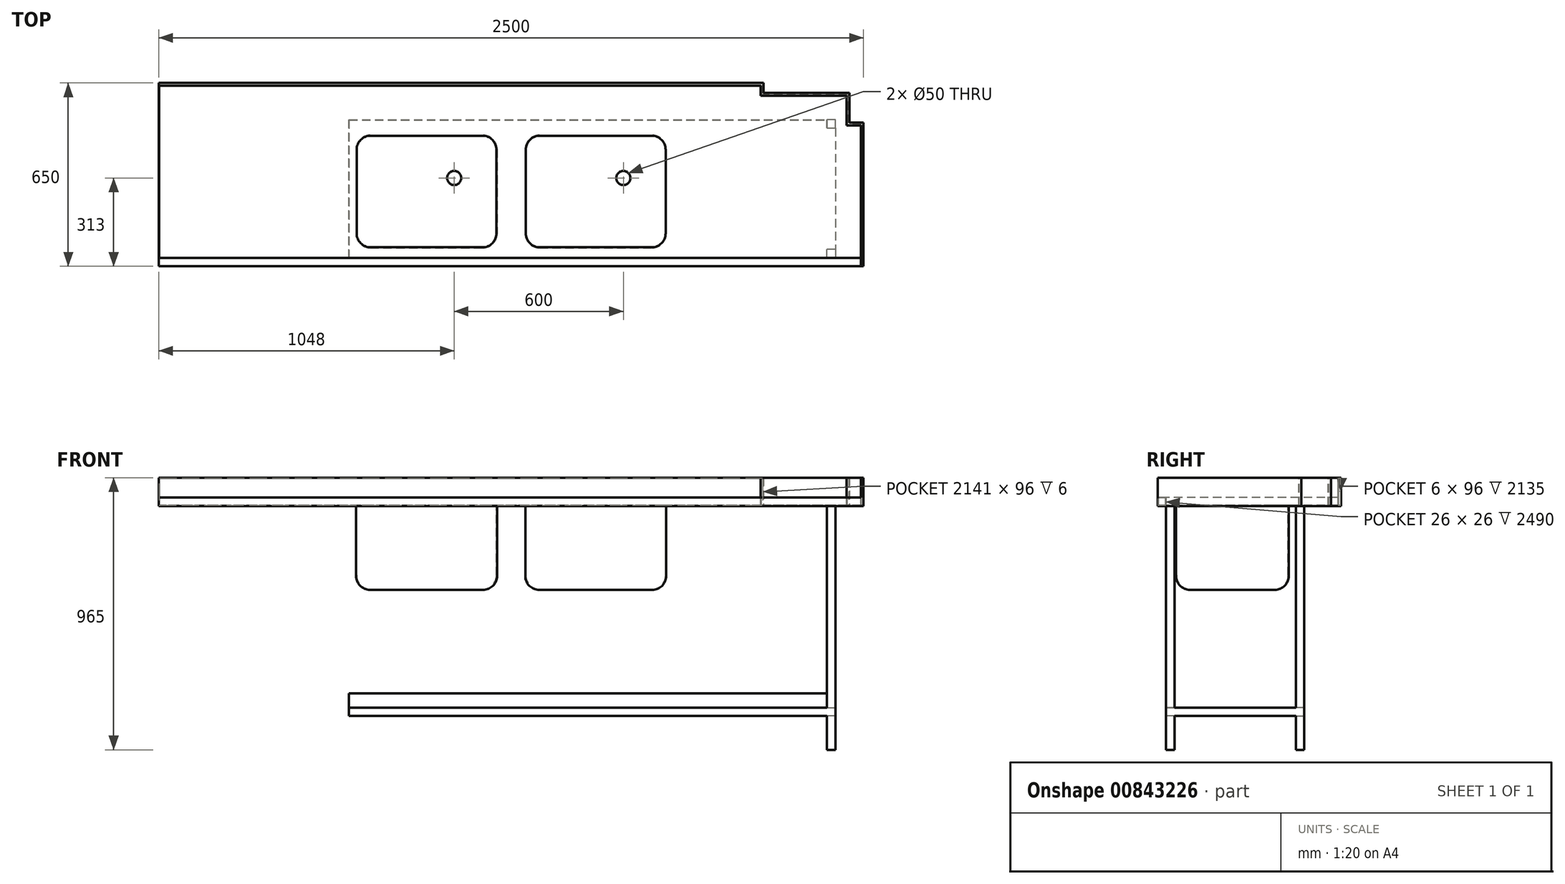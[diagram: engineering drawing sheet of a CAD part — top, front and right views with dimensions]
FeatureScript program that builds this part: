
annotation { "Feature Type Name" : "Feature", "Feature Type Description" : "" }
export const myFeature = defineFeature(function(context is Context, id is Id, definition is map)
    precondition{}
    {
        {
            var Q0;
            Q0=qCreatedBy(makeId("Top.planeOp"),FACE);
            var sketch = newSketch(context, id + "F0", { "sketchPlane" : qUnion([Q0])});
            skLineSegment(sketch, "E0", {"start": v(0, 0) * mm, "end": v(2500, 0) * mm});
            skLineSegment(sketch, "E1", {"start": v(2500, 0) * mm, "end": v(2500, 510) * mm});
            skLineSegment(sketch, "E2", {"start": v(2500, 510) * mm, "end": v(2450, 510) * mm});
            skLineSegment(sketch, "E3", {"start": v(2450, 510) * mm, "end": v(2450, 615) * mm});
            skLineSegment(sketch, "E4", {"start": v(2450, 615) * mm, "end": v(2145, 615) * mm});
            skLineSegment(sketch, "E5", {"start": v(2145, 615) * mm, "end": v(2145, 650) * mm});
            skLineSegment(sketch, "E6", {"start": v(2145, 650) * mm, "end": v(0, 650) * mm});
            skLineSegment(sketch, "E7", {"start": v(0, 650) * mm, "end": v(0, 0) * mm});
            skSolve(sketch);
        }
        {
            var Q0;
            Q0 = qSketchRegion(id + "F0", true);
            extrude(context, id + "F1", {"entities" : qUnion([Q0]), "depth" : 100 * mm, "offsetDistance" : 25 * mm});
        }
        {
            var Q0;
            Q0=makeQuery(id+"F1.opExtrude","CAP_FACE",FACE,{"disambiguationData":[OSD([sQuery(id+"F0.wireOp",EDGE,"E0"),sQuery(id+"F0.wireOp",EDGE,"E1"),sQuery(id+"F0.wireOp",EDGE,"E2"),sQuery(id+"F0.wireOp",EDGE,"E3"),sQuery(id+"F0.wireOp",EDGE,"E4"),sQuery(id+"F0.wireOp",EDGE,"E5"),sQuery(id+"F0.wireOp",EDGE,"E6"),sQuery(id+"F0.wireOp",EDGE,"E7")])],"isStart":false});
            var sketch = newSketch(context, id + "F2", { "sketchPlane" : qUnion([Q0])});
            skLineSegment(sketch, "E8", {"start": v(0, 30) * mm, "end": v(2490, 30) * mm});
            skLineSegment(sketch, "E9", {"start": v(2490, 500) * mm, "end": v(2440, 500) * mm});
            skLineSegment(sketch, "E10", {"start": v(2440, 500) * mm, "end": v(2440, 605) * mm});
            skLineSegment(sketch, "E11", {"start": v(2440, 605) * mm, "end": v(2135, 605) * mm});
            skLineSegment(sketch, "E12", {"start": v(2135, 605) * mm, "end": v(2135, 640) * mm});
            skLineSegment(sketch, "E13", {"start": v(2135, 640) * mm, "end": v(0, 640) * mm});
            skLineSegment(sketch, "E14", {"start": v(0, 640) * mm, "end": v(0, 30) * mm});
            skLineSegment(sketch, "E15", {"start": v(2490, 500) * mm, "end": v(2490, 30) * mm});
            skSolve(sketch);
        }
        {
            var Q0;
            Q0 = qSketchRegion(id + "F2", true);
            extrude(context, id + "F3", {"entities" : qUnion([Q0]), "operationType" : NewBodyOperationType.REMOVE, "oppositeDirection" : true, "depth" : 98 * mm, "offsetDistance" : 25 * mm});
        }
        {
            var Q0;
            Q0=makeQuery(id+"F3.boolean.opBoolean","COPY",FACE,{"derivedFrom":makeQuery(id+"F3.opExtrude","CAP_FACE",FACE,{"disambiguationData":[OSD([sQuery(id+"F2.wireOp",EDGE,"E8"),sQuery(id+"F2.wireOp",EDGE,"WZKGSPdI-TEh4-vyXV-Ibzs-68OWXZtWBOVU"),sQuery(id+"F2.wireOp",EDGE,"E9"),sQuery(id+"F2.wireOp",EDGE,"E10"),sQuery(id+"F2.wireOp",EDGE,"E11"),sQuery(id+"F2.wireOp",EDGE,"E12"),sQuery(id+"F2.wireOp",EDGE,"E13"),sQuery(id+"F2.wireOp",EDGE,"E14")])],"isStart":false})});
            var sketch = newSketch(context, id + "F4", { "sketchPlane" : qUnion([Q0])});
            skLineSegment(sketch, "E16.bottom", {"start": v(700, 465) * mm, "end": v(1200, 465) * mm});
            skLineSegment(sketch, "E16.top", {"start": v(700, 65) * mm, "end": v(1200, 65) * mm});
            skLineSegment(sketch, "E16.left", {"start": v(700, 465) * mm, "end": v(700, 65) * mm});
            skLineSegment(sketch, "E16.right", {"start": v(1200, 465) * mm, "end": v(1200, 65) * mm});
            skLineSegment(sketch, "E17.bottom", {"start": v(1300, 465) * mm, "end": v(1800, 465) * mm});
            skLineSegment(sketch, "E17.top", {"start": v(1300, 65) * mm, "end": v(1800, 65) * mm});
            skLineSegment(sketch, "E17.left", {"start": v(1300, 465) * mm, "end": v(1300, 65) * mm});
            skLineSegment(sketch, "E17.right", {"start": v(1800, 465) * mm, "end": v(1800, 65) * mm});
            skSolve(sketch);
        }
        {
            var Q0;
            Q0 = qSketchRegion(id + "F4", true);
            var Q1;
            Q1=makeQuery(id+"F4.imprint","IMPRINT",FACE,{"disambiguationData":[TD([[makeQuery(id+"F4.imprint","IMPRINT",EDGE,{"derivedFrom":sQuery(id+"F4.wireOp",EDGE,"0PvLLEWH-obXo-W6PY-pfR3-ScPsw102PUe8.bottom")}),-1.0]])]});
            var Q2;
            Q2=makeQuery(id+"F4.imprint","IMPRINT",FACE,{"disambiguationData":[TD([[makeQuery(id+"F4.imprint","IMPRINT",EDGE,{"derivedFrom":sQuery(id+"F4.wireOp",EDGE,"tlFFw7kf-LK7W-eKNi-DYG7-TUnyD2dlcll0.bottom")}),-1.0]])]});
            extrude(context, id + "F5", {"entities" : qUnion([Q0, Q1, Q2]), "operationType" : NewBodyOperationType.ADD, "oppositeDirection" : true, "depth" : 300 * mm, "offsetDistance" : 25 * mm});
        }
        {
            var Q0;
            Q0=makeQuery(id+"F1.opExtrude","CAP_FACE",FACE,{"disambiguationData":[OSD([sQuery(id+"F0.wireOp",EDGE,"E0"),sQuery(id+"F0.wireOp",EDGE,"E1"),sQuery(id+"F0.wireOp",EDGE,"E2"),sQuery(id+"F0.wireOp",EDGE,"E3"),sQuery(id+"F0.wireOp",EDGE,"E4"),sQuery(id+"F0.wireOp",EDGE,"E5"),sQuery(id+"F0.wireOp",EDGE,"E6"),sQuery(id+"F0.wireOp",EDGE,"E7")])],"isStart":false});
            var sketch = newSketch(context, id + "F6", { "sketchPlane" : qUnion([Q0])});
            skLineSegment(sketch, "E18.bottom", {"start": v(0, 30) * mm, "end": v(2490, 30) * mm});
            skLineSegment(sketch, "E18.top", {"start": v(0, 0) * mm, "end": v(2490, 0) * mm});
            skLineSegment(sketch, "E18.left", {"start": v(0, 30) * mm, "end": v(0, 0) * mm});
            skLineSegment(sketch, "E18.right", {"start": v(2490, 30) * mm, "end": v(2490, 0) * mm});
            skSolve(sketch);
        }
        {
            var Q0;
            Q0 = qSketchRegion(id + "F6", true);
            extrude(context, id + "F7", {"entities" : qUnion([Q0]), "operationType" : NewBodyOperationType.REMOVE, "oppositeDirection" : true, "depth" : 70 * mm, "offsetDistance" : 25 * mm});
        }
        {
            var Q0;
            Q0=makeQuery(id+"F3.boolean.opBoolean","COPY",FACE,{"derivedFrom":makeQuery(id+"F3.opExtrude","CAP_FACE",FACE,{"disambiguationData":[OSD([sQuery(id+"F2.wireOp",EDGE,"E8"),sQuery(id+"F2.wireOp",EDGE,"WZKGSPdI-TEh4-vyXV-Ibzs-68OWXZtWBOVU"),sQuery(id+"F2.wireOp",EDGE,"E9"),sQuery(id+"F2.wireOp",EDGE,"E10"),sQuery(id+"F2.wireOp",EDGE,"E11"),sQuery(id+"F2.wireOp",EDGE,"E12"),sQuery(id+"F2.wireOp",EDGE,"E13"),sQuery(id+"F2.wireOp",EDGE,"E14")])],"isStart":false})});
            shell(context, id + "F8", {"entities" : qUnion([Q0]), "thickness" : 2 * mm});
        }
        {
            var Q0;
            Q0=makeQuery(id+"F8.opShell","OFFSET_EDGE",EDGE,{"disambiguationData":[OSD([sQuery(id+"F4.wireOp",EDGE,"E16.bottom"),sQuery(id+"F4.wireOp",EDGE,"E16.left")])]});
            var Q1;
            Q1=makeQuery(id+"F8.opShell","OFFSET_EDGE",EDGE,{"disambiguationData":[OSD([sQuery(id+"F4.wireOp",EDGE,"E16.bottom"),sQuery(id+"F4.wireOp",EDGE,"E16.right")])]});
            var Q2;
            Q2=makeQuery(id+"F8.opShell","OFFSET_EDGE",EDGE,{"disambiguationData":[OSD([sQuery(id+"F4.wireOp",EDGE,"E16.bottom")])]});
            var Q3;
            Q3=makeQuery(id+"F8.opShell","OFFSET_EDGE",EDGE,{"disambiguationData":[OSD([sQuery(id+"F4.wireOp",EDGE,"E16.top"),sQuery(id+"F4.wireOp",EDGE,"E16.left")])]});
            var Q4;
            Q4=makeQuery(id+"F8.opShell","OFFSET_EDGE",EDGE,{"disambiguationData":[OSD([sQuery(id+"F4.wireOp",EDGE,"E16.top"),sQuery(id+"F4.wireOp",EDGE,"E16.right")])]});
            var Q5;
            Q5=makeQuery(id+"F8.opShell","OFFSET_EDGE",EDGE,{"disambiguationData":[OSD([sQuery(id+"F4.wireOp",EDGE,"E16.right")])]});
            var Q6;
            Q6=makeQuery(id+"F8.opShell","OFFSET_EDGE",EDGE,{"disambiguationData":[OSD([sQuery(id+"F4.wireOp",EDGE,"E16.top")])]});
            var Q7;
            Q7=makeQuery(id+"F8.opShell","OFFSET_EDGE",EDGE,{"disambiguationData":[OSD([sQuery(id+"F4.wireOp",EDGE,"E16.left")])]});
            var Q8;
            Q8=makeQuery(id+"F8.opShell","OFFSET_EDGE",EDGE,{"disambiguationData":[OSD([sQuery(id+"F4.wireOp",EDGE,"E17.left")])]});
            var Q9;
            Q9=makeQuery(id+"F8.opShell","OFFSET_EDGE",EDGE,{"disambiguationData":[OSD([sQuery(id+"F4.wireOp",EDGE,"E17.bottom"),sQuery(id+"F4.wireOp",EDGE,"E17.left")])]});
            var Q10;
            Q10=makeQuery(id+"F8.opShell","OFFSET_EDGE",EDGE,{"disambiguationData":[OSD([sQuery(id+"F4.wireOp",EDGE,"E17.bottom")])]});
            var Q11;
            Q11=makeQuery(id+"F8.opShell","OFFSET_EDGE",EDGE,{"disambiguationData":[OSD([sQuery(id+"F4.wireOp",EDGE,"E17.bottom"),sQuery(id+"F4.wireOp",EDGE,"E17.right")])]});
            var Q12;
            Q12=makeQuery(id+"F8.opShell","OFFSET_EDGE",EDGE,{"disambiguationData":[OSD([sQuery(id+"F4.wireOp",EDGE,"E17.right")])]});
            var Q13;
            Q13=makeQuery(id+"F8.opShell","OFFSET_EDGE",EDGE,{"disambiguationData":[OSD([sQuery(id+"F4.wireOp",EDGE,"E17.top"),sQuery(id+"F4.wireOp",EDGE,"E17.right")])]});
            var Q14;
            Q14=makeQuery(id+"F8.opShell","OFFSET_EDGE",EDGE,{"disambiguationData":[OSD([sQuery(id+"F4.wireOp",EDGE,"E17.top")])]});
            var Q15;
            Q15=makeQuery(id+"F8.opShell","OFFSET_EDGE",EDGE,{"disambiguationData":[OSD([sQuery(id+"F4.wireOp",EDGE,"E17.top"),sQuery(id+"F4.wireOp",EDGE,"E17.left")])]});
            var Q16;
            Q16=makeQuery(id+"F5.opExtrude","SWEPT_EDGE",EDGE,{"disambiguationData":[OSD([sQuery(id+"F4.wireOp",EDGE,"E16.top"),sQuery(id+"F4.wireOp",EDGE,"E16.left")])]});
            var Q17;
            Q17=makeQuery(id+"F5.opExtrude","CAP_EDGE",EDGE,{"disambiguationData":[OSD([sQuery(id+"F4.wireOp",EDGE,"E16.left")])],"isStart":false});
            var Q18;
            Q18=makeQuery(id+"F5.opExtrude","CAP_EDGE",EDGE,{"disambiguationData":[OSD([sQuery(id+"F4.wireOp",EDGE,"E16.top")])],"isStart":false});
            var Q19;
            Q19=makeQuery(id+"F5.opExtrude","SWEPT_EDGE",EDGE,{"disambiguationData":[OSD([sQuery(id+"F4.wireOp",EDGE,"E17.top"),sQuery(id+"F4.wireOp",EDGE,"E17.left")])]});
            var Q20;
            Q20=makeQuery(id+"F5.opExtrude","CAP_EDGE",EDGE,{"disambiguationData":[OSD([sQuery(id+"F4.wireOp",EDGE,"E17.left")])],"isStart":false});
            var Q21;
            Q21=makeQuery(id+"F5.opExtrude","CAP_EDGE",EDGE,{"disambiguationData":[OSD([sQuery(id+"F4.wireOp",EDGE,"E17.top")])],"isStart":false});
            var Q22;
            Q22=makeQuery(id+"F5.opExtrude","SWEPT_EDGE",EDGE,{"disambiguationData":[OSD([sQuery(id+"F4.wireOp",EDGE,"E16.top"),sQuery(id+"F4.wireOp",EDGE,"E16.right")])]});
            var Q23;
            Q23=makeQuery(id+"F5.opExtrude","CAP_EDGE",EDGE,{"disambiguationData":[OSD([sQuery(id+"F4.wireOp",EDGE,"E16.right")])],"isStart":false});
            var Q24;
            Q24=makeQuery(id+"F5.opExtrude","SWEPT_EDGE",EDGE,{"disambiguationData":[OSD([sQuery(id+"F4.wireOp",EDGE,"E17.top"),sQuery(id+"F4.wireOp",EDGE,"E17.right")])]});
            var Q25;
            Q25=makeQuery(id+"F5.opExtrude","CAP_EDGE",EDGE,{"disambiguationData":[OSD([sQuery(id+"F4.wireOp",EDGE,"E17.right")])],"isStart":false});
            var Q26;
            Q26=makeQuery(id+"F5.opExtrude","SWEPT_EDGE",EDGE,{"disambiguationData":[OSD([sQuery(id+"F4.wireOp",EDGE,"E17.bottom"),sQuery(id+"F4.wireOp",EDGE,"E17.right")])]});
            var Q27;
            Q27=makeQuery(id+"F5.opExtrude","CAP_EDGE",EDGE,{"disambiguationData":[OSD([sQuery(id+"F4.wireOp",EDGE,"E17.bottom")])],"isStart":false});
            var Q28;
            Q28=makeQuery(id+"F5.opExtrude","SWEPT_EDGE",EDGE,{"disambiguationData":[OSD([sQuery(id+"F4.wireOp",EDGE,"E17.bottom"),sQuery(id+"F4.wireOp",EDGE,"E17.left")])]});
            var Q29;
            Q29=makeQuery(id+"F5.opExtrude","SWEPT_EDGE",EDGE,{"disambiguationData":[OSD([sQuery(id+"F4.wireOp",EDGE,"E16.bottom"),sQuery(id+"F4.wireOp",EDGE,"E16.right")])]});
            var Q30;
            Q30=makeQuery(id+"F5.opExtrude","CAP_EDGE",EDGE,{"disambiguationData":[OSD([sQuery(id+"F4.wireOp",EDGE,"E16.bottom")])],"isStart":false});
            var Q31;
            Q31=makeQuery(id+"F5.opExtrude","SWEPT_EDGE",EDGE,{"disambiguationData":[OSD([sQuery(id+"F4.wireOp",EDGE,"E16.bottom"),sQuery(id+"F4.wireOp",EDGE,"E16.left")])]});
            fillet(context, id + "F9", {"entities" : qUnion([Q0, Q1, Q2, Q3, Q4, Q5, Q6, Q7, Q8, Q9, Q10, Q11, Q12, Q13, Q14, Q15, Q16, Q17, Q18, Q19, Q20, Q21, Q22, Q23, Q24, Q25, Q26, Q27, Q28, Q29, Q30, Q31]), "radius" : 50 * mm, "tangentPropagation" : true, "allowEdgeOverflow" : false});
        }
        {
            var Q0;
            Q0=makeQuery(id+"F8.opShell","OFFSET_FACE",FACE,{"disambiguationData":[OSD([sQuery(id+"F4.wireOp",EDGE,"E16.bottom"),sQuery(id+"F4.wireOp",EDGE,"E16.top"),sQuery(id+"F4.wireOp",EDGE,"E16.left"),sQuery(id+"F4.wireOp",EDGE,"E16.right")])]});
            var sketch = newSketch(context, id + "F10", { "sketchPlane" : qUnion([Q0])});
            skCircle(sketch, "E19", {"center": v(1048, 313) * mm, "radius": 25 * mm});
            skCircle(sketch, "E20", {"center": v(1648, 313) * mm, "radius": 25 * mm});
            skSolve(sketch);
        }
        {
            var Q0;
            Q0 = qSketchRegion(id + "F10", true);
            extrude(context, id + "F11", {"entities" : qUnion([Q0]), "operationType" : NewBodyOperationType.REMOVE, "endBound" : BoundingType.UP_TO_NEXT, "oppositeDirection" : true, "depth" : 25 * mm, "offsetDistance" : 25 * mm});
        }
        {
            var Q0;
            Q0=makeQuery(id+"F1.opExtrude","CAP_FACE",FACE,{"disambiguationData":[OSD([sQuery(id+"F0.wireOp",EDGE,"E0"),sQuery(id+"F0.wireOp",EDGE,"E1"),sQuery(id+"F0.wireOp",EDGE,"E2"),sQuery(id+"F0.wireOp",EDGE,"E3"),sQuery(id+"F0.wireOp",EDGE,"E4"),sQuery(id+"F0.wireOp",EDGE,"E5"),sQuery(id+"F0.wireOp",EDGE,"E6"),sQuery(id+"F0.wireOp",EDGE,"E7")])],"isStart":true});
            var sketch = newSketch(context, id + "F12", { "sketchPlane" : qUnion([Q0])});
            skLineSegment(sketch, "E21.bottom", {"start": v(2400, -490) * mm, "end": v(2370, -490) * mm});
            skLineSegment(sketch, "E21.top", {"start": v(2400, -520) * mm, "end": v(2370, -520) * mm});
            skLineSegment(sketch, "E21.left", {"start": v(2400, -490) * mm, "end": v(2400, -520) * mm});
            skLineSegment(sketch, "E21.right", {"start": v(2370, -490) * mm, "end": v(2370, -520) * mm});
            skPoint(sketch, "E21.middle", {"position": v(2385, -505) * mm});
            skLineSegment(sketch, "E22.bottom", {"start": v(2370, -60) * mm, "end": v(2400, -60) * mm});
            skLineSegment(sketch, "E22.top", {"start": v(2370, -30) * mm, "end": v(2400, -30) * mm});
            skLineSegment(sketch, "E22.left", {"start": v(2370, -60) * mm, "end": v(2370, -30) * mm});
            skLineSegment(sketch, "E22.right", {"start": v(2400, -60) * mm, "end": v(2400, -30) * mm});
            skPoint(sketch, "E22.middle", {"position": v(2385, -45) * mm});
            skSolve(sketch);
        }
        {
            var Q0;
            Q0 = qSketchRegion(id + "F12", true);
            extrude(context, id + "F13", {"entities" : qUnion([Q0]), "operationType" : NewBodyOperationType.ADD, "depth" : 865 * mm, "offsetDistance" : 25 * mm});
        }
        {
            var Q0;
            Q0=makeQuery(id+"F8.opShell","OFFSET_EDGE",EDGE,{"disambiguationData":[OSD([sQuery(id+"F0.wireOp",EDGE,"E0"),sQuery(id+"F0.wireOp",EDGE,"E1"),sQuery(id+"F0.wireOp",EDGE,"E2"),sQuery(id+"F0.wireOp",EDGE,"E3"),sQuery(id+"F0.wireOp",EDGE,"E4"),sQuery(id+"F0.wireOp",EDGE,"E5"),sQuery(id+"F0.wireOp",EDGE,"E6"),sQuery(id+"F0.wireOp",EDGE,"E7"),sQuery(id+"F4.wireOp",EDGE,"E16.bottom")])]});
            var Q1;
            Q1=makeQuery(id+"F8.opShell","OFFSET_EDGE",EDGE,{"disambiguationData":[OSD([sQuery(id+"F0.wireOp",EDGE,"E0"),sQuery(id+"F0.wireOp",EDGE,"E1"),sQuery(id+"F0.wireOp",EDGE,"E2"),sQuery(id+"F0.wireOp",EDGE,"E3"),sQuery(id+"F0.wireOp",EDGE,"E4"),sQuery(id+"F0.wireOp",EDGE,"E5"),sQuery(id+"F0.wireOp",EDGE,"E6"),sQuery(id+"F0.wireOp",EDGE,"E7"),sQuery(id+"F4.wireOp",EDGE,"E17.bottom")])]});
            fillet(context, id + "F14", {"entities" : qUnion([Q0, Q1]), "radius" : 6 * mm, "tangentPropagation" : true, "allowEdgeOverflow" : false});
        }
        {
            var Q0;
            Q0=makeQuery(id+"F3.boolean.opBoolean","COPY",FACE,{"derivedFrom":makeQuery(id+"F3.opExtrude","SWEPT_FACE",FACE,{"disambiguationData":[OSD([sQuery(id+"F2.wireOp",EDGE,"E8")])]})});
            var sketch = newSketch(context, id + "F15", { "sketchPlane" : qUnion([Q0])});
            skLineSegment(sketch, "E23.bottom", {"start": v(0, 30) * mm, "end": v(-2, 30) * mm});
            skLineSegment(sketch, "E23.top", {"start": v(0, 2) * mm, "end": v(-2, 2) * mm});
            skLineSegment(sketch, "E23.left", {"start": v(0, 30) * mm, "end": v(0, 2) * mm});
            skLineSegment(sketch, "E23.right", {"start": v(-2, 30) * mm, "end": v(-2, 2) * mm});
            skSolve(sketch);
        }
        {
            var Q0;
            Q0 = qSketchRegion(id + "F15", true);
            extrude(context, id + "F16", {"entities" : qUnion([Q0]), "operationType" : NewBodyOperationType.ADD, "endBound" : BoundingType.UP_TO_NEXT, "depth" : 25 * mm, "offsetDistance" : 25 * mm});
        }
        {
            var Q0;
            Q0=makeQuery(id+"F13.opExtrude","SWEPT_FACE",FACE,{"disambiguationData":[OSD([sQuery(id+"F12.wireOp",EDGE,"E22.right")])]});
            var sketch = newSketch(context, id + "F17", { "sketchPlane" : qUnion([Q0])});
            skLineSegment(sketch, "E24", {"start": v(520, -745) * mm, "end": v(520, -665) * mm});
            skLineSegment(sketch, "E25", {"start": v(520, -665) * mm, "end": v(518, -665) * mm});
            skLineSegment(sketch, "E26", {"start": v(518, -665) * mm, "end": v(518, -715) * mm});
            skLineSegment(sketch, "E27", {"start": v(518, -715) * mm, "end": v(30, -715) * mm});
            skLineSegment(sketch, "E28", {"start": v(30, -715) * mm, "end": v(30, -745) * mm});
            skLineSegment(sketch, "E29", {"start": v(30, -745) * mm, "end": v(520, -745) * mm});
            skPoint(sketch, "E30.orphan", {"position": v(520, -715) * mm});
            skSolve(sketch);
        }
        {
            var Q0;
            Q0 = qSketchRegion(id + "F17", true);
            extrude(context, id + "F18", {"entities" : qUnion([Q0]), "operationType" : NewBodyOperationType.ADD, "oppositeDirection" : true, "depth" : 1725 * mm, "offsetDistance" : 25 * mm});
        }
    });
